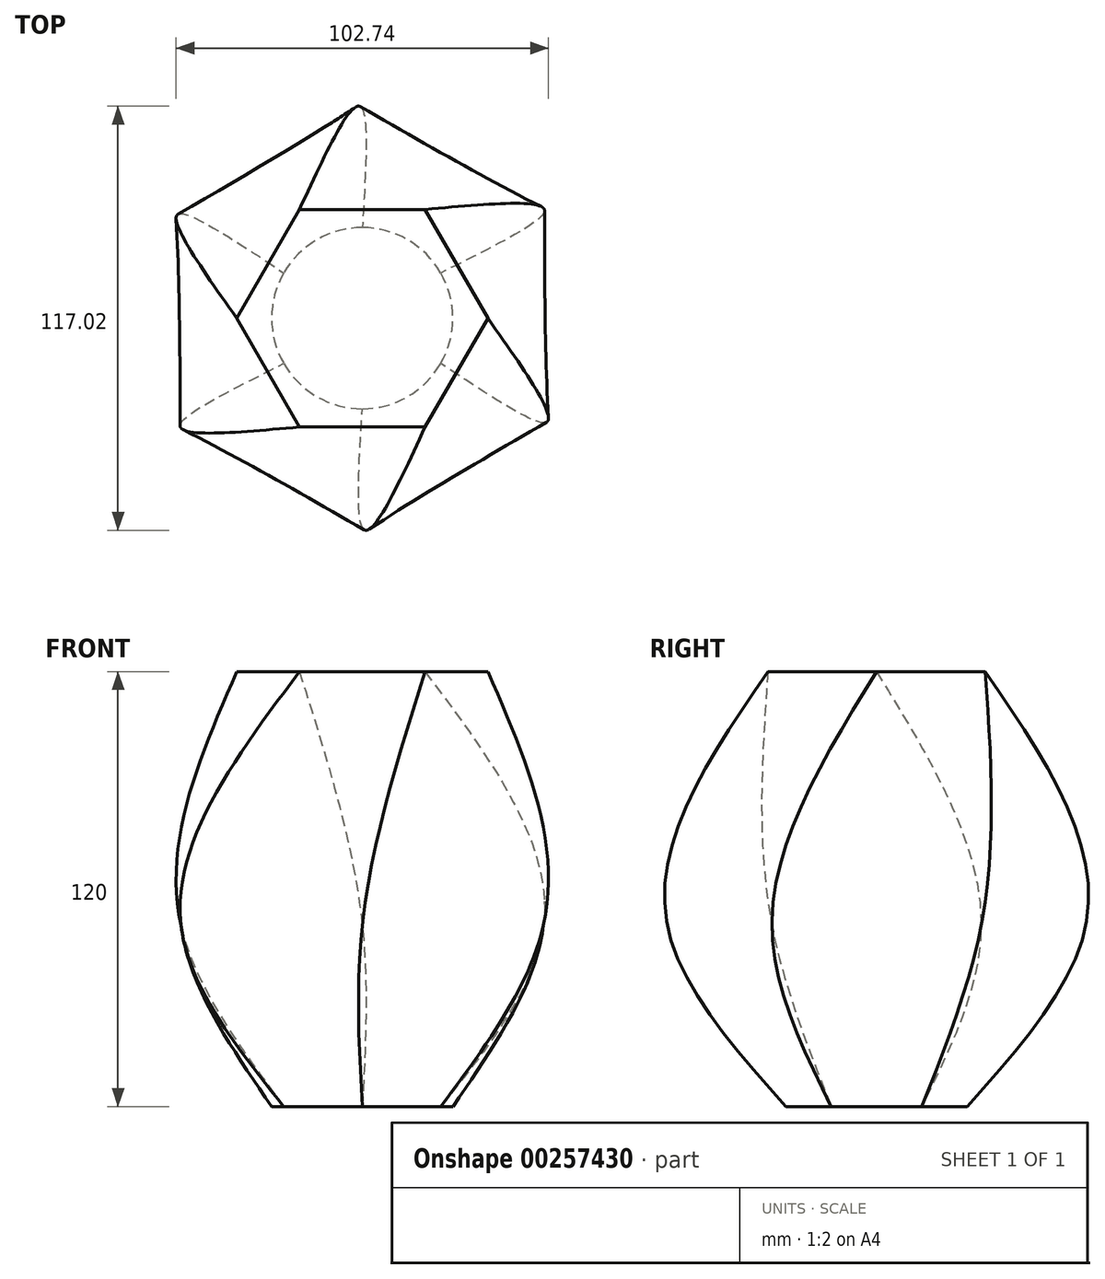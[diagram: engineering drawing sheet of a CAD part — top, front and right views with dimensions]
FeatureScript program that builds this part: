
annotation { "Feature Type Name" : "Feature", "Feature Type Description" : "" }
export const myFeature = defineFeature(function(context is Context, id is Id, definition is map)
    precondition{}
    {
        {
            var Q0;
            Q0=qCreatedBy(makeId("Top.planeOp"),FACE);
            var sketch = newSketch(context, id + "F0", { "sketchPlane" : qUnion([Q0])});
            skCircle(sketch, "E0", {"center": v(0, 0) * mm, "radius": 25 * mm});
            skSolve(sketch);
        }
        {
            var Q0;
            Q0=qCreatedBy(makeId("Top.planeOp"),FACE);
            cPlane(context, id + "F1", {"entities" : qUnion([Q0]), "cplaneType" : CPlaneType.OFFSET, "offset" : 50 * mm, "width" : 150 * mm, "height" : 150 * mm});
        }
        {
            var Q0;
            Q0=qCreatedBy(id+"F1.planeOp",FACE);
            var sketch = newSketch(context, id + "F2", { "sketchPlane" : qUnion([Q0])});
            skCircle(sketch, "E1.cCircle", {"center": v(0, 0) * mm, "radius": 50 * mm, "construction": true});
            skLineSegment(sketch, "E1.0", {"start": v(-50, 28.87) * mm, "end": v(0, 57.74) * mm});
            skLineSegment(sketch, "E1.1", {"start": v(0, 57.74) * mm, "end": v(50, 28.87) * mm});
            skLineSegment(sketch, "E1.2", {"start": v(50, 28.87) * mm, "end": v(50, -28.87) * mm});
            skLineSegment(sketch, "E1.3", {"start": v(50, -28.87) * mm, "end": v(0, -57.74) * mm});
            skLineSegment(sketch, "E1.4", {"start": v(0, -57.74) * mm, "end": v(-50, -28.87) * mm});
            skLineSegment(sketch, "E1.5", {"start": v(-50, -28.87) * mm, "end": v(-50, 28.87) * mm});
            skPoint(sketch, "E1.0.midPoint", {"position": v(-25, 43.3) * mm});
            skSolve(sketch);
        }
        {
            var Q0;
            Q0=qCreatedBy(id+"F1.planeOp",FACE);
            cPlane(context, id + "F3", {"entities" : qUnion([Q0]), "cplaneType" : CPlaneType.OFFSET, "offset" : 70 * mm, "width" : 150 * mm, "height" : 150 * mm});
        }
        {
            var Q0;
            Q0=qCreatedBy(id+"F3.planeOp",FACE);
            var sketch = newSketch(context, id + "F4", { "sketchPlane" : qUnion([Q0])});
            skCircle(sketch, "E2.cCircle", {"center": v(0, 0) * mm, "radius": 30 * mm, "construction": true});
            skLineSegment(sketch, "E2.0", {"start": v(-17.32, 30) * mm, "end": v(17.32, 30) * mm});
            skLineSegment(sketch, "E2.1", {"start": v(17.32, 30) * mm, "end": v(34.64, 0) * mm});
            skLineSegment(sketch, "E2.2", {"start": v(34.64, 0) * mm, "end": v(17.32, -30) * mm});
            skLineSegment(sketch, "E2.3", {"start": v(17.32, -30) * mm, "end": v(-17.32, -30) * mm});
            skLineSegment(sketch, "E2.4", {"start": v(-17.32, -30) * mm, "end": v(-34.64, 0) * mm});
            skLineSegment(sketch, "E2.5", {"start": v(-34.64, 0) * mm, "end": v(-17.32, 30) * mm});
            skPoint(sketch, "E2.0.midPoint", {"position": v(0, 30) * mm});
            skSolve(sketch);
        }
        {
            var Q0;
            Q0=makeQuery(id+"F4.imprint","IMPRINT",FACE,{"disambiguationData":[TD([[makeQuery(id+"F4.imprint","IMPRINT",EDGE,{"derivedFrom":sQuery(id+"F4.wireOp",EDGE,"E2.0")}),-1.0]])]});
            var Q1;
            Q1=makeQuery(id+"F2.imprint","IMPRINT",FACE,{"disambiguationData":[TD([[makeQuery(id+"F2.imprint","IMPRINT",EDGE,{"derivedFrom":sQuery(id+"F2.wireOp",EDGE,"E1.0")}),-1.0]])]});
            var Q2;
            Q2=makeQuery(id+"F0.imprint","IMPRINT",FACE,{"disambiguationData":[TD([[makeQuery(id+"F0.imprint","IMPRINT",EDGE,{"derivedFrom":sQuery(id+"F0.wireOp",EDGE,"E0")}),1.0]])]});
            loft(context, id + "F5", {"sheetProfilesArray" : [{ "sheetProfileEntities" : qUnion([Q0]) }, { "sheetProfileEntities" : qUnion([Q1]) }, { "sheetProfileEntities" : qUnion([Q2]) }]});
        }
    });
